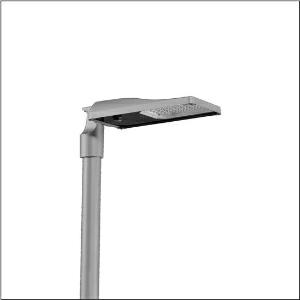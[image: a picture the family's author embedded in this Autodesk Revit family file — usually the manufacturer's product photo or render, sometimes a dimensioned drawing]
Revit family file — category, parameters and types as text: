
# Revit family: streetlight_sl_31_mini___st1_0a_5xh6d31r08ga_9a85
name_source: partatom
category: Lighting Fixtures
units: mm (PartAtom-declared; Revit-internal decimal feet)

## family parameters
Cut with Voids When Loaded = No
Host = Face
Light Source = No
Part Type = Normal
Room Calculation Point = No
Round Connector Dimension = Use Diameter
Shared = No

## types (1)
- --- (1 x LED, 5880 lm, 39.3 W, 3000K)
    Apparent Load = 39 VA
    CIE Flux Codes = 37 72 97 100 100
    Color Rendering = 70
    Color Temperature = 3000K
    Default Elevation = 1800 mm
    Description = Streetlight SL 31 mini, mast luminaire, primary light control with lens, of PMMA, primary optical cover: cover, of toughened safety glass, transparent, light distribution: ST1.0a, light emission: direct distribution, primary light characteristic: asymmetric, installation type: post-top, side-entry, LED, High Power LED, rated luminous flux: 5.880lm, luminous efficacy: 150lm/W, light colour: 730, colour temperature: 3000K, control: presetting dimming logarithmic, flexible luminous flux parameterisation, time-dependent luminous flux control, constant luminous flux control, power reduction, intelligent temperature release in ECG and LED module, overheat protection, with cable H07RN-F 2x 1.5mm², mains connection: 220..240V, AC, 50/60Hz, connection cable pre-assembled, cable length: 6,5m, start of lifetime: 39W, end of service life: 41W, reduction: 18W, luminaire housing, of diecast aluminium, powder-coated, Siteco® metallic grey (DB 702S), corrosivity category C5 high according to DIN EN ISO 12944, sealing non-destructively replaceable, multi-level sealing system, mast flange (76/60mm) included as standard, inclination: -15°..+20° (post-top) | -20°..+20° (side-entry), adjustable in 5° steps, no sealing on luminaire upper side, Smart Interface below, protection rating (complete): IP66, insulation class (complete): insulation class II (safety insulation), certification: CE, ENEC, ENEC+, VDE, UKCA, ZD4i, impact resistance: IK09, permissible operating ambient temperature for outdoor applications: -40..+50°C, standard-compliant lighting for roads and squares, packaging unit: 1 piece

Light Distribution: ST1.0a
    Height = 76 mm
    Lamp = 1 x LED
    Lamp Light Flux = 5880 lm
    Lamp Power = 39.3 W
    Lamp count = 1
    Length = 547 mm
    Luminous efficacy = 150 lm/W
    Manufacturer = Siteco
    ModVariant = No
    Model = 5XH6D31R08GA
    Number of Poles = 1
    OnlyDefault = Yes
    Power Factor = 1
    Product Name = Streetlight SL 31 mini | ST1.0a
    Product group = mast luminaire | pylon top
    ProductGroupID = 6100
    Protection Class = Protection class II
    Protection Degree = IP 66
    RLX_Detail_Level = 1
    RLX_Emergency_Light_Flux = 0 lm
    RLX_Emergency_Type = 0
    RLX_Emergency_Type_DB = No
    RlxData = <blob elided: 40069 chars, md5=3b471497>
    Socket = socket
    Standby Power = 0 W
    System Light Flux = 5880 lm
    System Power = 39 W
    Type Comments = factory setting: luminous flux: 100 % | dim-lin: 254 | 798 mA
    Type Image = l_1300328.jpg
    URL = http://relux.com
    VarID = @adj_012065
    Voltage = 0 V
    Weight = 0.00 kg
    Width = 265 mm

## geometry (parser evidence)
native form markers: Blend x4, Sweep x9
no freeform markers — native parametric forms only
